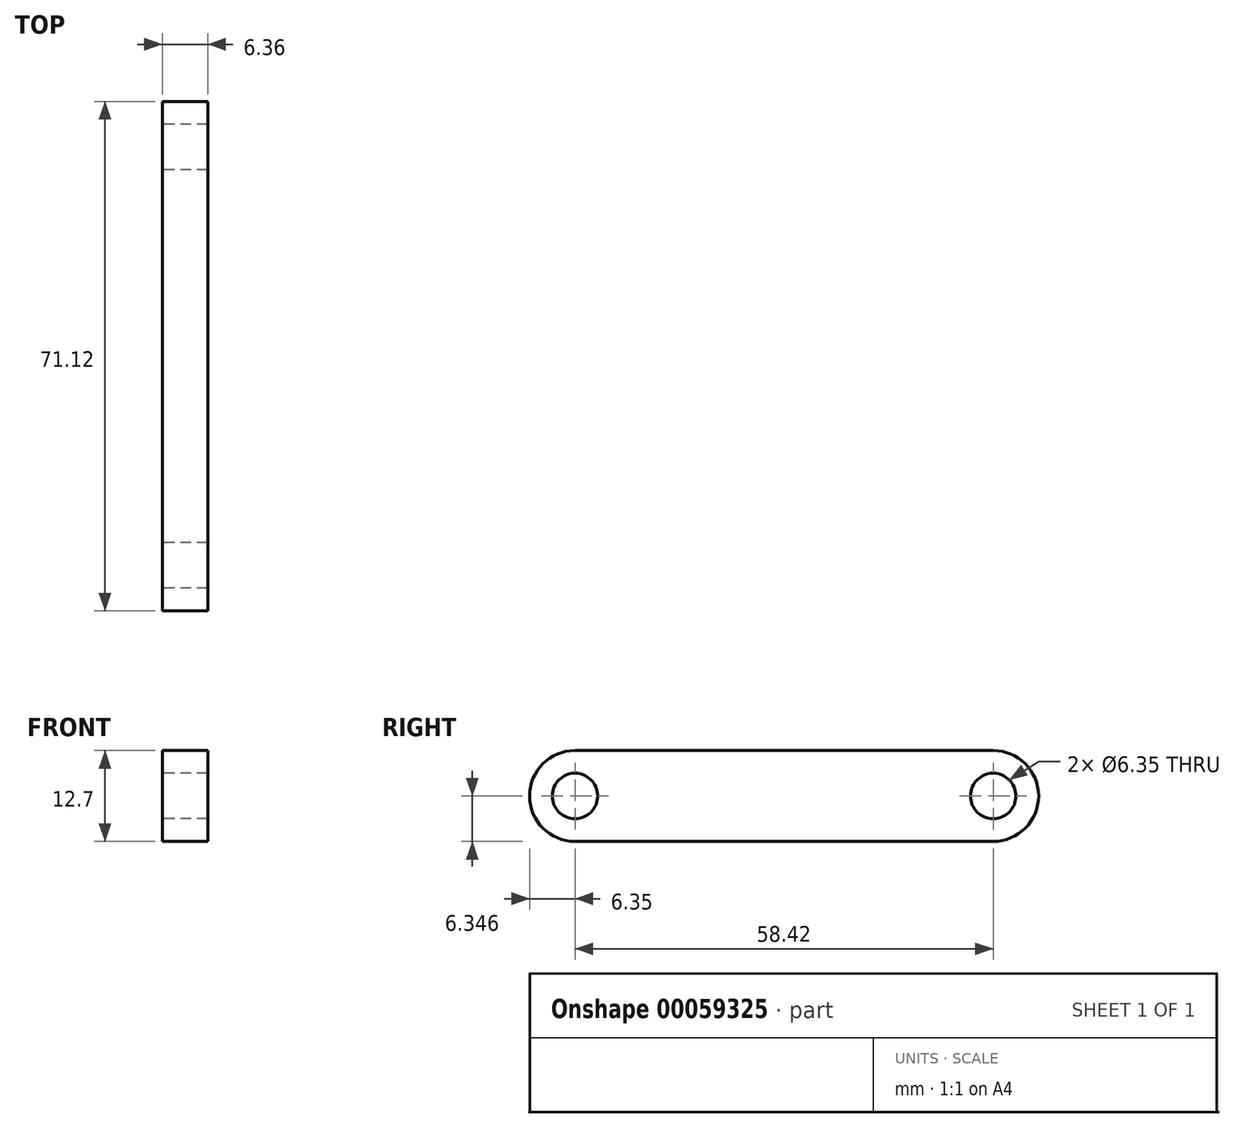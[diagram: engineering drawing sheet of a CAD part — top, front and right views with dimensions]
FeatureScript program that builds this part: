
annotation { "Feature Type Name" : "Feature", "Feature Type Description" : "" }
export const myFeature = defineFeature(function(context is Context, id is Id, definition is map)
    precondition{}
    {
        {
            var Q0;
            Q0=qCreatedBy(makeId("Right.planeOp"),FACE);
            var sketch = newSketch(context, id + "F0", { "sketchPlane" : qUnion([Q0])});
            skLineSegment(sketch, "E0.bottom", {"start": v(-29.2, 6.88) * mm, "end": v(29.21, 6.88) * mm});
            skLineSegment(sketch, "E0.top", {"start": v(-29.2, -5.82) * mm, "end": v(29.21, -5.82) * mm});
            skArc(sketch, "E1", {"start": v(-29.2, 6.88) * mm, "mid": v(-35.56, 0.53) * mm, "end": v(-29.2, -5.82) * mm});
            skArc(sketch, "E2", {"start": v(29.21, -5.82) * mm, "mid": v(35.56, 0.53) * mm, "end": v(29.21, 6.88) * mm});
            skCircle(sketch, "E3", {"center": v(-29.2, 0.53) * mm, "radius": 3.18 * mm});
            skCircle(sketch, "E4", {"center": v(29.21, 0.53) * mm, "radius": 3.18 * mm});
            skSolve(sketch);
        }
        {
            var Q0;
            Q0 = qSketchRegion(id + "F0", true);
            extrude(context, id + "F1", {"entities" : qUnion([Q0]), "endBound" : BoundingType.SYMMETRIC, "depth" : 6.35 * mm});
        }
    });
